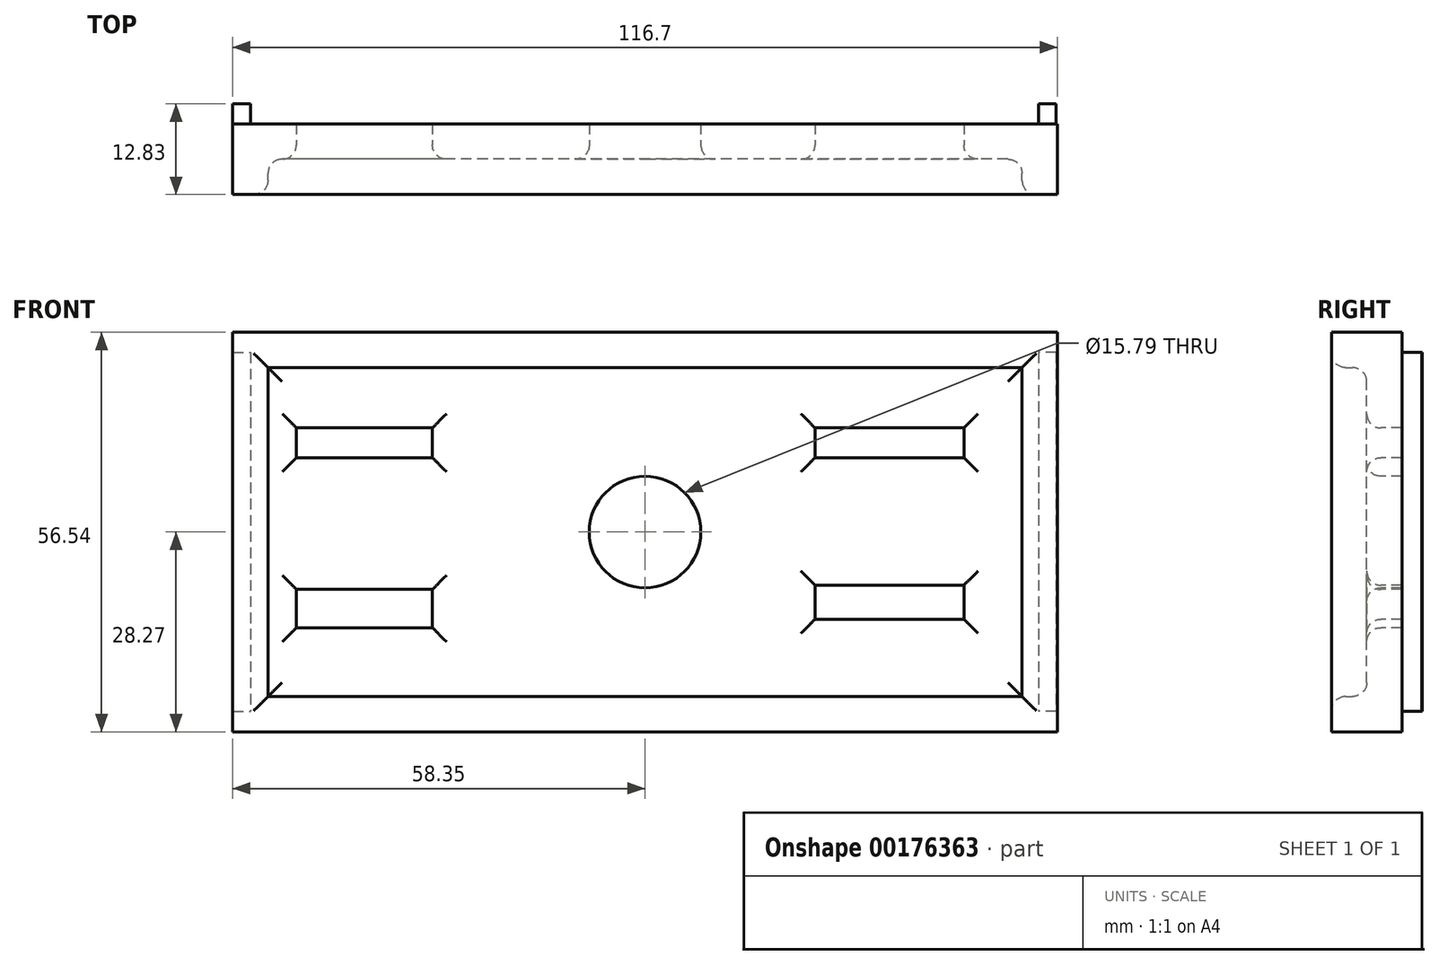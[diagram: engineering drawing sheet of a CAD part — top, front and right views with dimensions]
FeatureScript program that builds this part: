
annotation { "Feature Type Name" : "Feature", "Feature Type Description" : "" }
export const myFeature = defineFeature(function(context is Context, id is Id, definition is map)
    precondition{}
    {
        {
            var Q0;
            Q0=qCreatedBy(makeId("Front.planeOp"),FACE);
            var sketch = newSketch(context, id + "F0", { "sketchPlane" : qUnion([Q0])});
            skLineSegment(sketch, "E0.bottom", {"start": v(58.35, -28.27) * mm, "end": v(-58.35, -28.27) * mm});
            skLineSegment(sketch, "E0.top", {"start": v(58.35, 28.27) * mm, "end": v(-58.35, 28.27) * mm});
            skLineSegment(sketch, "E0.left", {"start": v(58.35, -28.27) * mm, "end": v(58.35, 28.27) * mm});
            skLineSegment(sketch, "E0.right", {"start": v(-58.35, -28.27) * mm, "end": v(-58.35, 28.27) * mm});
            skPoint(sketch, "E0.middle", {"position": v(0, 0) * mm});
            skSolve(sketch);
        }
        {
            var Q0;
            Q0 = qSketchRegion(id + "F0", true);
            extrude(context, id + "F1", {"entities" : qUnion([Q0]), "depth" : 10 * mm});
        }
        {
            var Q0;
            Q0=makeQuery(id+"F1.opExtrude","CAP_FACE",FACE,{"disambiguationData":[OSD([sQuery(id+"F0.wireOp",EDGE,"E0.bottom"),sQuery(id+"F0.wireOp",EDGE,"E0.top"),sQuery(id+"F0.wireOp",EDGE,"E0.left"),sQuery(id+"F0.wireOp",EDGE,"E0.right")])],"isStart":false});
            shell(context, id + "F2", {"entities" : qUnion([Q0]), "thickness" : 5 * mm});
        }
        {
            var Q0;
            Q0=makeQuery(id+"F2.opShell","OFFSET_FACE",FACE,{"disambiguationData":[OSD([sQuery(id+"F0.wireOp",EDGE,"E0.bottom"),sQuery(id+"F0.wireOp",EDGE,"E0.top"),sQuery(id+"F0.wireOp",EDGE,"E0.left"),sQuery(id+"F0.wireOp",EDGE,"E0.right")])]});
            var sketch = newSketch(context, id + "F3", { "sketchPlane" : qUnion([Q0])});
            skCircle(sketch, "E1", {"center": v(0, 0) * mm, "radius": 7.9 * mm});
            skLineSegment(sketch, "E2.bottom", {"start": v(-30.08, 10.53) * mm, "end": v(-49.33, 10.53) * mm});
            skLineSegment(sketch, "E2.top", {"start": v(-30.08, 14.74) * mm, "end": v(-49.33, 14.74) * mm});
            skLineSegment(sketch, "E2.left", {"start": v(-30.08, 10.53) * mm, "end": v(-30.08, 14.74) * mm});
            skLineSegment(sketch, "E2.right", {"start": v(-49.33, 10.53) * mm, "end": v(-49.33, 14.74) * mm});
            skPoint(sketch, "E2.middle", {"position": v(-39.7, 12.63) * mm});
            skLineSegment(sketch, "E3.bottom", {"start": v(-30.08, -13.54) * mm, "end": v(-49.33, -13.54) * mm});
            skLineSegment(sketch, "E3.top", {"start": v(-30.08, -8.12) * mm, "end": v(-49.33, -8.12) * mm});
            skLineSegment(sketch, "E3.left", {"start": v(-30.08, -13.54) * mm, "end": v(-30.08, -8.12) * mm});
            skLineSegment(sketch, "E3.right", {"start": v(-49.33, -13.54) * mm, "end": v(-49.33, -8.12) * mm});
            skPoint(sketch, "E3.middle", {"position": v(-39.7, -10.83) * mm});
            skPoint(sketch, "E3.middle.positionSnap0", {"position": v(-39.7, 10.53) * mm});
            skPoint(sketch, "E3.centerSnap0", {"position": v(-39.7, 10.53) * mm});
            skLineSegment(sketch, "E4.bottom", {"start": v(24.06, 10.53) * mm, "end": v(45.12, 10.53) * mm});
            skLineSegment(sketch, "E4.top", {"start": v(24.06, 14.74) * mm, "end": v(45.12, 14.74) * mm});
            skLineSegment(sketch, "E4.left", {"start": v(24.06, 10.53) * mm, "end": v(24.06, 14.74) * mm});
            skLineSegment(sketch, "E4.right", {"start": v(45.12, 10.53) * mm, "end": v(45.12, 14.74) * mm});
            skPoint(sketch, "E4.middle", {"position": v(34.6, 12.63) * mm});
            skLineSegment(sketch, "E5.bottom", {"start": v(24.06, -7.52) * mm, "end": v(45.12, -7.52) * mm});
            skLineSegment(sketch, "E5.top", {"start": v(24.06, -12.33) * mm, "end": v(45.12, -12.33) * mm});
            skLineSegment(sketch, "E5.left", {"start": v(24.06, -7.52) * mm, "end": v(24.06, -12.33) * mm});
            skLineSegment(sketch, "E5.right", {"start": v(45.12, -7.52) * mm, "end": v(45.12, -12.33) * mm});
            skPoint(sketch, "E5.middle", {"position": v(34.6, -9.93) * mm});
            skPoint(sketch, "E5.middle.positionSnap0", {"position": v(34.6, 10.53) * mm});
            skPoint(sketch, "E5.centerSnap0", {"position": v(34.6, 10.53) * mm});
            skSolve(sketch);
        }
        {
            var Q0;
            Q0=makeQuery(id+"F3.imprint","IMPRINT",FACE,{"disambiguationData":[TD([[makeQuery(id+"F3.imprint","IMPRINT",EDGE,{"derivedFrom":sQuery(id+"F3.wireOp",EDGE,"E2.bottom")}),-1.0]])]});
            var Q1;
            Q1 = qSketchRegion(id + "F3", true);
            extrude(context, id + "F4", {"entities" : qUnion([Q0, Q1]), "operationType" : NewBodyOperationType.REMOVE, "endBound" : BoundingType.THROUGH_ALL, "oppositeDirection" : true, "depth" : 25.4 * mm});
        }
        {
            var Q0;
            {var subQ0=sQuery(id+"F0.wireOp",EDGE,"E0.top");Q0=makeQuery(id+"F2.opShell","OFFSET_EDGE",EDGE,{"disambiguationData":[OSD([subQ0]),TDD([makeQuery(id+"F1.opExtrude","CAP_EDGE",EDGE,{"disambiguationData":[OSD([subQ0])],"isStart":false})])]});}
            var Q1;
            {var subQ0=sQuery(id+"F0.wireOp",EDGE,"E0.right");Q1=makeQuery(id+"F2.opShell","OFFSET_EDGE",EDGE,{"disambiguationData":[OSD([subQ0]),TDD([makeQuery(id+"F1.opExtrude","CAP_EDGE",EDGE,{"disambiguationData":[OSD([subQ0])],"isStart":false})])]});}
            var Q2;
            Q2=makeQuery(id+"F2.opShell","OFFSET_FACE",FACE,{"disambiguationData":[OSD([sQuery(id+"F0.wireOp",EDGE,"E0.bottom"),sQuery(id+"F0.wireOp",EDGE,"E0.top"),sQuery(id+"F0.wireOp",EDGE,"E0.left"),sQuery(id+"F0.wireOp",EDGE,"E0.right")])]});
            var Q3;
            {var subQ0=sQuery(id+"F0.wireOp",EDGE,"E0.left");Q3=makeQuery(id+"F2.opShell","OFFSET_EDGE",EDGE,{"disambiguationData":[OSD([subQ0]),TDD([makeQuery(id+"F1.opExtrude","CAP_EDGE",EDGE,{"disambiguationData":[OSD([subQ0])],"isStart":false})])]});}
            var Q4;
            {var subQ0=sQuery(id+"F0.wireOp",EDGE,"E0.bottom");Q4=makeQuery(id+"F2.opShell","OFFSET_EDGE",EDGE,{"disambiguationData":[OSD([subQ0]),TDD([makeQuery(id+"F1.opExtrude","CAP_EDGE",EDGE,{"disambiguationData":[OSD([subQ0])],"isStart":false})])]});}
            fillet(context, id + "F5", {"entities" : qUnion([Q0, Q1, Q2, Q3, Q4]), "radius" : 2 * mm, "tangentPropagation" : true, "allowEdgeOverflow" : false});
        }
        {
            var Q0;
            Q0=qCreatedBy(makeId("Top.planeOp"),FACE);
            var sketch = newSketch(context, id + "F6", { "sketchPlane" : qUnion([Q0])});
            skLineSegment(sketch, "E6.bottom", {"start": v(-58.33, 0) * mm, "end": v(-55.83, 0) * mm});
            skLineSegment(sketch, "E6.top", {"start": v(-58.33, 2.83) * mm, "end": v(-55.83, 2.83) * mm});
            skLineSegment(sketch, "E6.left", {"start": v(-58.33, 0) * mm, "end": v(-58.33, 2.83) * mm});
            skLineSegment(sketch, "E6.right", {"start": v(-55.83, 0) * mm, "end": v(-55.83, 2.83) * mm});
            skLineSegment(sketch, "E7.bottom", {"start": v(58.16, 0) * mm, "end": v(55.68, 0) * mm});
            skLineSegment(sketch, "E7.top", {"start": v(58.16, 2.8) * mm, "end": v(55.68, 2.8) * mm});
            skLineSegment(sketch, "E7.left", {"start": v(58.16, 0) * mm, "end": v(58.16, 2.8) * mm});
            skLineSegment(sketch, "E7.right", {"start": v(55.68, 0) * mm, "end": v(55.68, 2.8) * mm});
            skSolve(sketch);
        }
        {
            var Q0;
            Q0=makeQuery(id+"F6.imprint","IMPRINT",FACE,{"disambiguationData":[TD([[makeQuery(id+"F6.imprint","IMPRINT",EDGE,{"derivedFrom":sQuery(id+"F6.wireOp",EDGE,"E6.bottom")}),1.0]])]});
            extrude(context, id + "F7", {"entities" : qUnion([Q0]), "operationType" : NewBodyOperationType.ADD, "depth" : 25.4 * mm});
        }
        {
            var Q0;
            Q0=qCreatedBy(makeId("Top.planeOp"),FACE);
            var sketch = newSketch(context, id + "F8", { "sketchPlane" : qUnion([Q0])});
            skLineSegment(sketch, "E8.bottom", {"start": v(58.19, 0) * mm, "end": v(55.7, 0) * mm});
            skLineSegment(sketch, "E8.top", {"start": v(58.19, 2.82) * mm, "end": v(55.7, 2.82) * mm});
            skLineSegment(sketch, "E8.left", {"start": v(58.19, 0) * mm, "end": v(58.19, 2.82) * mm});
            skLineSegment(sketch, "E8.right", {"start": v(55.7, 0) * mm, "end": v(55.7, 2.82) * mm});
            skSolve(sketch);
        }
        {
            var Q0;
            Q0=makeQuery(id+"F8.imprint","IMPRINT",FACE,{"disambiguationData":[TD([[makeQuery(id+"F8.imprint","IMPRINT",EDGE,{"derivedFrom":sQuery(id+"F8.wireOp",EDGE,"E8.bottom")}),-1.0]])]});
            extrude(context, id + "F9", {"entities" : qUnion([Q0]), "operationType" : NewBodyOperationType.ADD, "depth" : 25.4 * mm});
        }
        {
            var Q0;
            Q0=makeQuery(id+"F9.opExtrude","CAP_FACE",FACE,{"disambiguationData":[OSD([sQuery(id+"F8.wireOp",EDGE,"E8.bottom"),sQuery(id+"F8.wireOp",EDGE,"E8.top"),sQuery(id+"F8.wireOp",EDGE,"E8.left"),sQuery(id+"F8.wireOp",EDGE,"E8.right")])],"isStart":true});
            extrude(context, id + "F10", {"entities" : qUnion([Q0]), "operationType" : NewBodyOperationType.ADD, "depth" : 25.4 * mm});
        }
        {
            var Q0;
            Q0=makeQuery(id+"F7.opExtrude","CAP_FACE",FACE,{"disambiguationData":[OSD([sQuery(id+"F6.wireOp",EDGE,"E6.bottom"),sQuery(id+"F6.wireOp",EDGE,"E6.top"),sQuery(id+"F6.wireOp",EDGE,"E6.left"),sQuery(id+"F6.wireOp",EDGE,"E6.right")])],"isStart":true});
            extrude(context, id + "F11", {"entities" : qUnion([Q0]), "operationType" : NewBodyOperationType.ADD, "depth" : 25.4 * mm});
        }
    });
